# Revit family: Fixture_Support_Horizontal-Back-to-Back-Zurn-Z1201-ND4-XH
name_source: partatom
category: Plumbing Fixtures
units: mm (PartAtom-declared; Revit-internal decimal feet)

## family parameters
Always vertical = Yes
Cut with Voids When Loaded = No
Maintain Annotation Orientation = No
OmniClass Number = 23.45.55.11
OmniClass Title = Sanitary Components
Part Type = Normal
Room Calculation Point = No
Round Connector Dimension = Use Radius
Shared = No
Work Plane-Based = No

## types (1)
- Fixture_Support_Horizontal-Back-to-Back-Zurn-Z1201-ND4-XH
    Approx. Weight (Lbs) = 142.00
    Assembly Code = D2030400
    CW Connection = No
    CWFU = 0
    Default Elevation = 0 "
    Description = EXTRA-HEAVY-DUTY - 750 lbs [340kg] BACK-TO-BACK EZCARRY® ADJUSTABLE HORIZONTAL HIGH PERFORMANCE SIPHON JET NO-HUB WATER CLOSET CARRIER SYSTEM
    HW Connection = No
    HWFU = 0
    Horizantal Pipe Diameter (Actual) = 4.5 "
    Horizantal Pipe Diameter (Nominal) = 4 "
    K DIM = 4.125 "
    Main Material = Iron - Zurn -Cast - Painted - Blue
    Manufacturer = Zurn Water, LLC
    Manufacurer Brand = Zurn
    Model = Z1201-ND4-XH
    Modified Date = 08/09/2024
    N_Distance Bwtween Two Carriers = 13.188 "
    Product Documentation Link = https://www.zurn.com
    Product Installation Sheet URL = https://www.zurn.com
    Product Page URL = https://www.zurn.com
    Product data url = https://www.bimobject.com
    Sanitary Inlet Radius = 2 "
    Sanitary Outlet Radius = 2 "
    URL = www.zurn.com
    Vent Connection = Yes
    Vent Connection Radius = 1 "
    Vent Diameter (Actual) = 2.375 "
    Vent Diameter (Nominal) = 2 "
    WFU = 0
    Waste Connection = Yes
    Water Closet Inlet Radius = 1.5 "

## geometry (parser evidence)
native form markers: Sweep x12
no freeform markers — native parametric forms only
